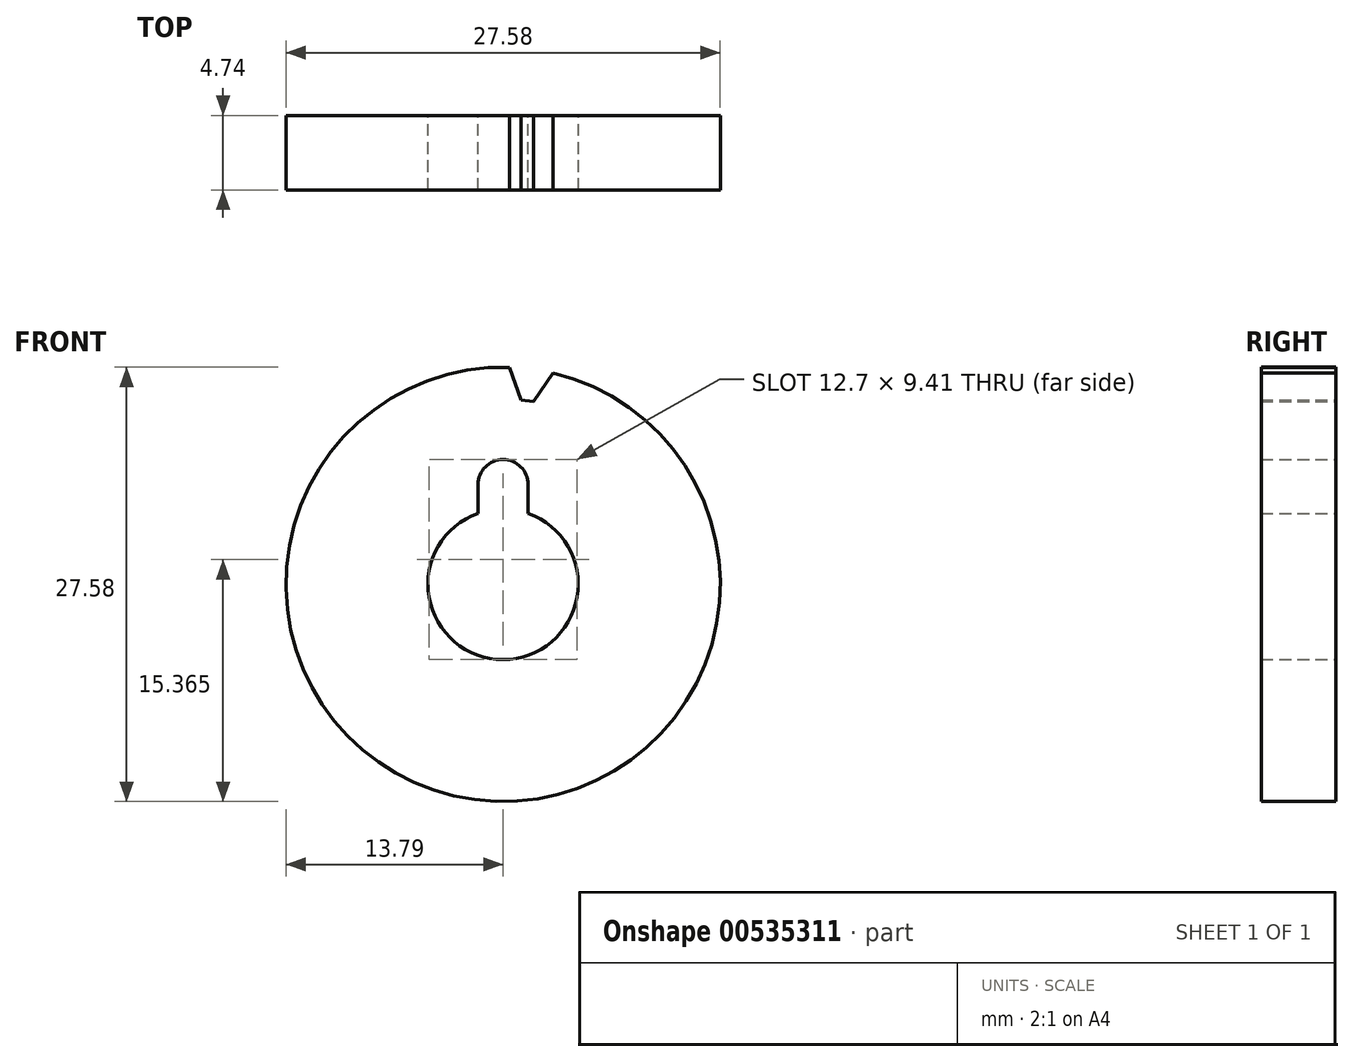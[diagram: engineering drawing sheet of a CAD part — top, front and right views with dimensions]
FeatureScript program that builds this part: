
annotation { "Feature Type Name" : "Feature", "Feature Type Description" : "" }
export const myFeature = defineFeature(function(context is Context, id is Id, definition is map)
    precondition{}
    {
        {
            var Q0;
            Q0=qCreatedBy(makeId("Front.planeOp"),FACE);
            var sketch = newSketch(context, id + "F0", { "sketchPlane" : qUnion([Q0])});
            skCircle(sketch, "E0", {"center": v(0, 0) * mm, "radius": 4.78 * mm});
            skCircle(sketch, "E1", {"center": v(0, 0) * mm, "radius": 13.8 * mm});
            skSolve(sketch);
        }
        {
            var Q0;
            Q0 = qSketchRegion(id + "F0", true);
            extrude(context, id + "F1", {"entities" : qUnion([Q0]), "depth" : 4.74 * mm, "offsetDistance" : 25.4 * mm});
        }
        {
            var Q0;
            Q0=qCreatedBy(makeId("Front.planeOp"),FACE);
            var sketch = newSketch(context, id + "F2", { "sketchPlane" : qUnion([Q0])});
            skLineSegment(sketch, "E2.bottom", {"start": v(-1.59, 0) * mm, "end": v(1.59, 0) * mm});
            skLineSegment(sketch, "E2.left", {"start": v(-1.59, 0) * mm, "end": v(-1.59, 6.34) * mm});
            skLineSegment(sketch, "E2.right", {"start": v(1.59, 0) * mm, "end": v(1.59, 6.34) * mm});
            skArc(sketch, "E3", {"start": v(1.59, 6.34) * mm, "mid": v(0, 7.92) * mm, "end": v(-1.59, 6.34) * mm});
            skLineSegment(sketch, "E4", {"start": v(0, 7.92) * mm, "end": v(0, -4.78) * mm, "construction": true});
            skSolve(sketch);
        }
        {
            var Q0;
            Q0 = qSketchRegion(id + "F2", true);
            extrude(context, id + "F3", {"entities" : qUnion([Q0]), "operationType" : NewBodyOperationType.REMOVE, "endBound" : BoundingType.THROUGH_ALL, "depth" : 25.4 * mm, "offsetDistance" : 25.4 * mm});
        }
        {
            var Q0;
            Q0=qCreatedBy(makeId("Front.planeOp"),FACE);
            var sketch = newSketch(context, id + "F4", { "sketchPlane" : qUnion([Q0])});
            skCircle(sketch, "E5", {"center": v(0, 0) * mm, "radius": 11.76 * mm, "construction": true});
            skLineSegment(sketch, "E6", {"start": v(-0.4, 13.8) * mm, "end": v(0.4, 13.8) * mm, "construction": true});
            skLineSegment(sketch, "E7", {"start": v(0, 13.8) * mm, "end": v(0, 0) * mm, "construction": true});
            skLineSegment(sketch, "E8", {"start": v(1.13, 11.71) * mm, "end": v(1.94, 11.6) * mm});
            skLineSegment(sketch, "E9", {"start": v(1.54, 11.66) * mm, "end": v(0, 0) * mm, "construction": true});
            skLineSegment(sketch, "E10", {"start": v(0.4, 13.8) * mm, "end": v(1.13, 11.71) * mm});
            skLineSegment(sketch, "E11", {"start": v(1.94, 11.6) * mm, "end": v(3.18, 13.43) * mm});
            skArc(sketch, "E12", {"start": v(3.18, 13.43) * mm, "mid": v(1.8, 13.72) * mm, "end": v(0.4, 13.8) * mm});
            skSolve(sketch);
        }
        {
            var Q0;
            Q0 = qSketchRegion(id + "F4", true);
            extrude(context, id + "F5", {"entities" : qUnion([Q0]), "operationType" : NewBodyOperationType.REMOVE, "endBound" : BoundingType.THROUGH_ALL, "depth" : 25.4 * mm, "offsetDistance" : 25.4 * mm});
        }
    });
